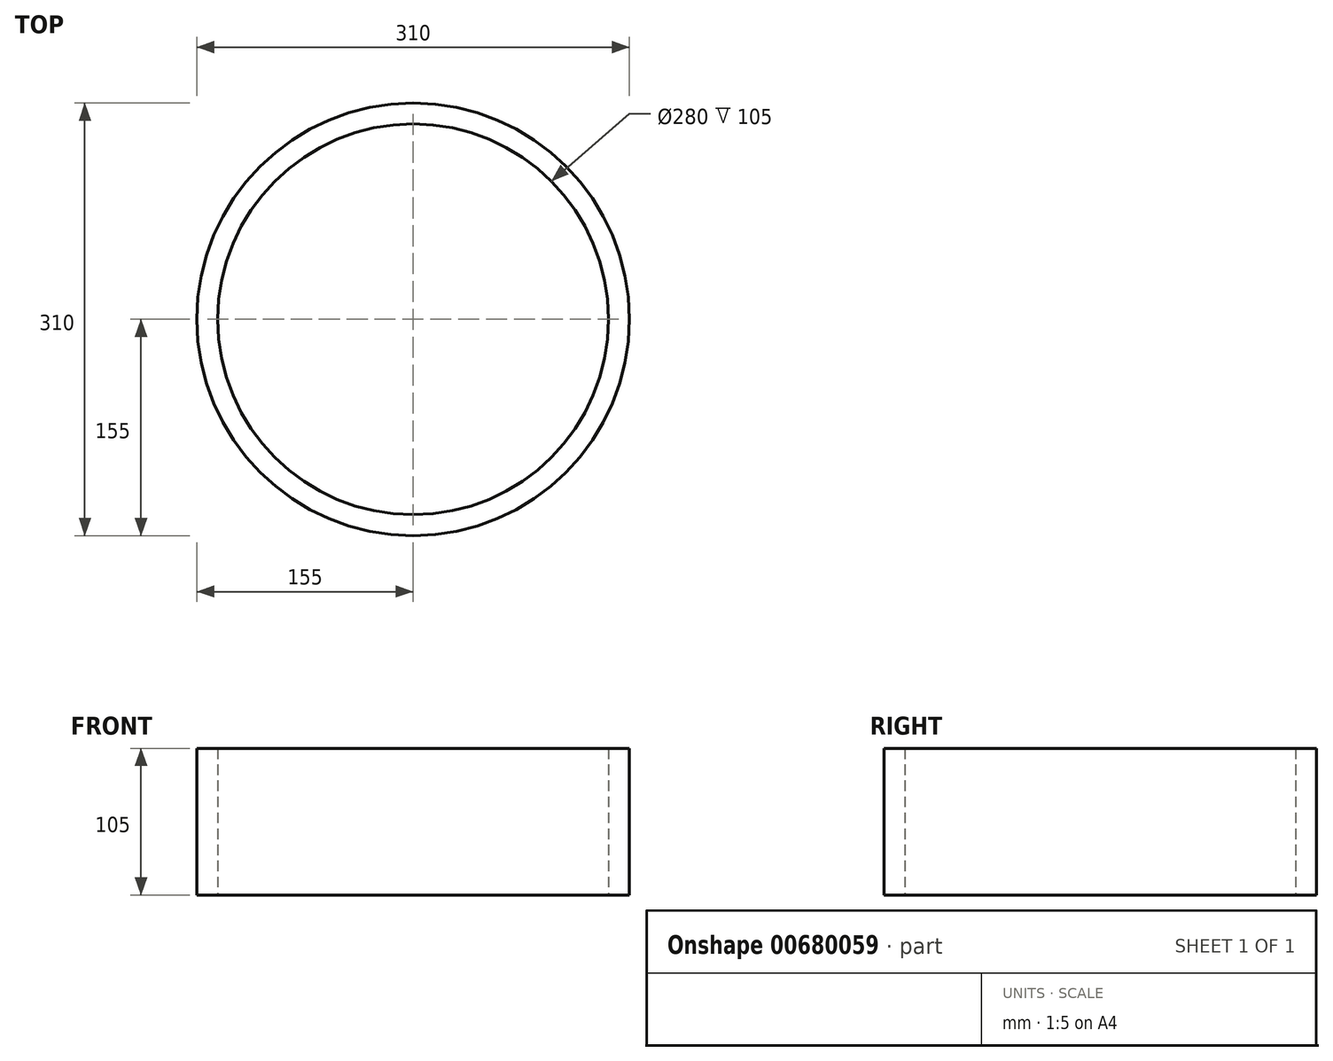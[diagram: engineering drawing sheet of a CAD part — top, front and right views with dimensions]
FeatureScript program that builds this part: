
annotation { "Feature Type Name" : "Feature", "Feature Type Description" : "" }
export const myFeature = defineFeature(function(context is Context, id is Id, definition is map)
    precondition{}
    {
        {
            var Q0;
            Q0=qCreatedBy(makeId("Top.planeOp"),FACE);
            var sketch = newSketch(context, id + "F0", { "sketchPlane" : qUnion([Q0])});
            skCircle(sketch, "E0", {"center": v(0, 0) * mm, "radius": 155 * mm});
            skCircle(sketch, "E1", {"center": v(0, 0) * mm, "radius": 140 * mm});
            skSolve(sketch);
        }
        {
            var Q0;
            Q0=qSketchRegion(id+"F0",true);
            extrude(context, id + "F1", {"entities" : qUnion([Q0]), "depth" : 105 * mm});
        }
    });
